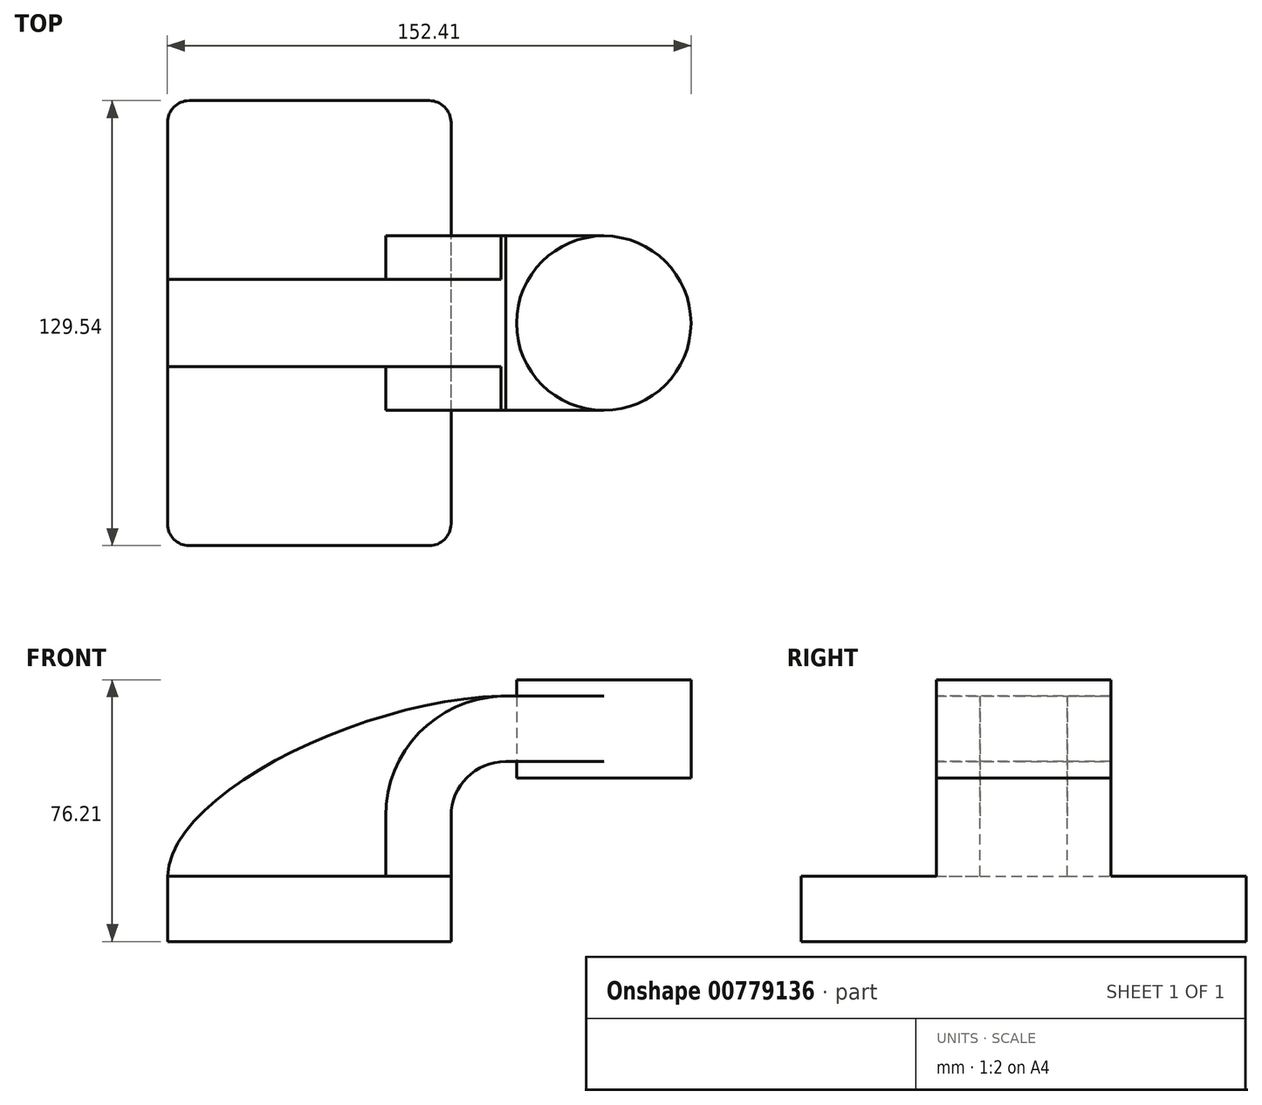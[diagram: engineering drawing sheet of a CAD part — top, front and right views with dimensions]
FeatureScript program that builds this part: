
annotation { "Feature Type Name" : "Feature", "Feature Type Description" : "" }
export const myFeature = defineFeature(function(context is Context, id is Id, definition is map)
    precondition{}
    {
        {
            var Q0;
            Q0=qCreatedBy(makeId("Front.planeOp"),FACE);
            var sketch = newSketch(context, id + "F0", { "sketchPlane" : qUnion([Q0])});
            skLineSegment(sketch, "E0.bottom", {"start": v(41.28, -9.52) * mm, "end": v(-41.27, -9.53) * mm});
            skLineSegment(sketch, "E0.top", {"start": v(41.27, 9.53) * mm, "end": v(-41.28, 9.52) * mm});
            skLineSegment(sketch, "E0.left", {"start": v(41.28, -9.52) * mm, "end": v(41.27, 9.53) * mm});
            skLineSegment(sketch, "E0.right", {"start": v(-41.27, -9.53) * mm, "end": v(-41.28, 9.52) * mm});
            skPoint(sketch, "E0.middle", {"position": v(0, 0) * mm});
            skLineSegment(sketch, "E1.bottom", {"start": v(111.12, 38.1) * mm, "end": v(60.32, 38.1) * mm});
            skLineSegment(sketch, "E1.top", {"start": v(111.12, 66.68) * mm, "end": v(60.32, 66.68) * mm});
            skLineSegment(sketch, "E1.left", {"start": v(111.12, 38.1) * mm, "end": v(111.12, 66.68) * mm});
            skLineSegment(sketch, "E1.right", {"start": v(60.32, 38.1) * mm, "end": v(60.32, 66.68) * mm});
            skPoint(sketch, "E1.middle", {"position": v(85.72, 52.39) * mm});
            skLineSegment(sketch, "E2", {"start": v(41.27, 9.53) * mm, "end": v(41.27, 26.99) * mm});
            skArc(sketch, "E3", {"start": v(41.27, 26.99) * mm, "mid": v(45.92, 38.21) * mm, "end": v(57.15, 42.86) * mm});
            skLineSegment(sketch, "E4", {"start": v(57.15, 42.86) * mm, "end": v(85.72, 42.86) * mm});
            skLineSegment(sketch, "E5.0", {"start": v(57.15, 61.91) * mm, "end": v(85.72, 61.91) * mm});
            skArc(sketch, "E5.1", {"start": v(22.22, 26.99) * mm, "mid": v(32.45, 51.68) * mm, "end": v(57.15, 61.91) * mm});
            skLineSegment(sketch, "E5.2", {"start": v(22.22, 9.53) * mm, "end": v(22.22, 26.99) * mm});
            skLineSegment(sketch, "E6", {"start": v(85.72, 38.1) * mm, "end": v(85.72, 66.68) * mm});
            skFitSpline(sketch, "E7", {"points": [v(-41.28, 9.52) * mm, v(57.15, 61.91) * mm], "startDerivative": vector(2.88, 73.36) * mm, "endDerivative": vector(121.28, 1.41) * mm});
            skSolve(sketch);
        }
        {
            var Q0;
            Q0=makeQuery(id+"F0.imprint","IMPRINT",FACE,{"disambiguationData":[TD([[makeQuery(id+"F0.imprint","IMPRINT",EDGE,{"derivedFrom":sQuery(id+"F0.wireOp",EDGE,"E0.bottom")}),-1.0]])]});
            extrude(context, id + "F1", {"entities" : qUnion([Q0]), "endBound" : BoundingType.SYMMETRIC, "depth" : 129.54 * mm, "offsetDistance" : 25.4 * mm});
        }
        {
            var Q0;
            {var subQ1=sQuery(id+"F0.wireOp",EDGE,"E2");Q0=makeQuery(id+"F0.imprint","IMPRINT",FACE,{"disambiguationData":[TD([[makeQuery(id+"F0.imprint","IMPRINT",EDGE,{"derivedFrom":subQ1}),1.0]])]});}
            var Q1;
            {var subQ0=sQuery(id+"F0.wireOp",EDGE,"E4");var subQ1=sQuery(id+"F0.wireOp",EDGE,"E1.right");var subQ2=makeQuery(id+"F0.imprint","INTERSECT",VERTEX,{"derivedFrom":[subQ1,subQ0]});Q1=makeQuery(id+"F0.imprint","IMPRINT",FACE,{"disambiguationData":[TD([[makeQuery(id+"F0.imprint","IMPRINT",EDGE,{"disambiguationData":[TD([[subQ2,-1.0]])],"derivedFrom":subQ1}),-1.0]])]});}
            extrude(context, id + "F2", {"entities" : qUnion([Q0, Q1]), "operationType" : NewBodyOperationType.ADD, "endBound" : BoundingType.SYMMETRIC, "depth" : 50.8 * mm, "offsetDistance" : 25.4 * mm});
        }
        {
            var Q0;
            {var subQ3=sQuery(id+"F0.wireOp",EDGE,"E5.2");Q0=makeQuery(id+"F0.imprint","IMPRINT",FACE,{"disambiguationData":[TD([[makeQuery(id+"F0.imprint","IMPRINT",EDGE,{"derivedFrom":subQ3}),1.0]])]});}
            extrude(context, id + "F3", {"entities" : qUnion([Q0]), "operationType" : NewBodyOperationType.ADD, "endBound" : BoundingType.SYMMETRIC, "depth" : 25.4 * mm, "offsetDistance" : 25.4 * mm});
        }
        {
            var Q0;
            {var subQ0=sQuery(id+"F0.wireOp",EDGE,"E1.left");Q0=makeQuery(id+"F0.imprint","IMPRINT",FACE,{"disambiguationData":[TD([[makeQuery(id+"F0.imprint","IMPRINT",EDGE,{"derivedFrom":subQ0}),1.0]])]});}
            var Q1;
            Q1=sQuery(id+"F0.wireOp",EDGE,"E6");
            revolve(context, id + "F4", {"surfaceOperationType" : NewSurfaceOperationType.NEW, "entities" : qUnion([Q0]), "axis" : qUnion([Q1]), "revolveType" : RevolveType.FULL});
        }
        {
            var Q0;
            Q0=makeQuery(id+"F1.opExtrude","CAP_EDGE",EDGE,{"disambiguationData":[OSD([sQuery(id+"F0.wireOp",EDGE,"E0.left")])],"isStart":false});
            var Q1;
            Q1=makeQuery(id+"F1.opExtrude","CAP_EDGE",EDGE,{"disambiguationData":[OSD([sQuery(id+"F0.wireOp",EDGE,"E0.right")])],"isStart":false});
            var Q2;
            Q2=makeQuery(id+"F1.opExtrude","CAP_EDGE",EDGE,{"disambiguationData":[OSD([sQuery(id+"F0.wireOp",EDGE,"E0.right")])],"isStart":true});
            var Q3;
            Q3=makeQuery(id+"F1.opExtrude","CAP_EDGE",EDGE,{"disambiguationData":[OSD([sQuery(id+"F0.wireOp",EDGE,"E0.left")])],"isStart":true});
            fillet(context, id + "F5", {"entities" : qUnion([Q0, Q1, Q2, Q3]), "radius" : 6.35 * mm, "tangentPropagation" : true, "allowEdgeOverflow" : false});
        }
    });
